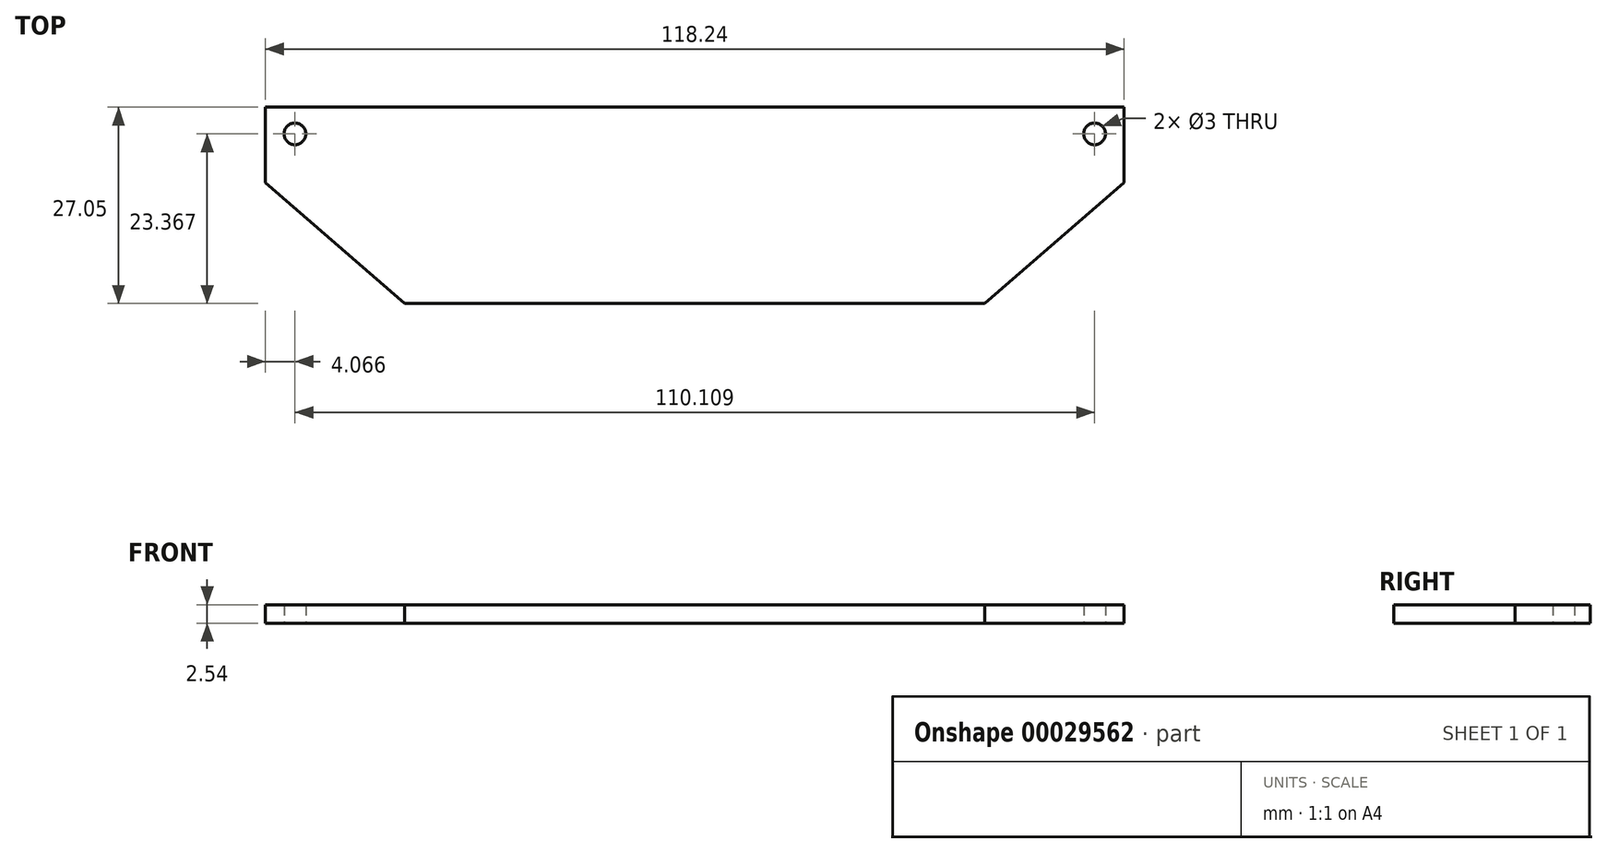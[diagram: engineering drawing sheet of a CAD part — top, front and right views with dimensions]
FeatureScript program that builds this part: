
annotation { "Feature Type Name" : "Feature", "Feature Type Description" : "" }
export const myFeature = defineFeature(function(context is Context, id is Id, definition is map)
    precondition{}
    {
        {
            var Q0;
            Q0=qCreatedBy(makeId("Top.planeOp"),FACE);
            var sketch = newSketch(context, id + "F0", { "sketchPlane" : qUnion([Q0])});
            skLineSegment(sketch, "E0", {"start": v(-59.12, 0) * mm, "end": v(59.12, 0) * mm});
            skPoint(sketch, "E1", {"position": v(0, 0) * mm});
            skLineSegment(sketch, "E2", {"start": v(-59.12, 0) * mm, "end": v(-59.12, -10.4) * mm});
            skLineSegment(sketch, "E3", {"start": v(-59.12, -10.4) * mm, "end": v(-39.94, -27.05) * mm});
            skLineSegment(sketch, "E4", {"start": v(-39.94, -27.05) * mm, "end": v(39.94, -27.05) * mm});
            skLineSegment(sketch, "E5", {"start": v(39.94, -27.05) * mm, "end": v(59.12, -10.4) * mm});
            skLineSegment(sketch, "E6", {"start": v(59.12, -10.4) * mm, "end": v(59.12, 0) * mm});
            skPoint(sketch, "E7", {"position": v(0, -27.05) * mm});
            skCircle(sketch, "E8", {"center": v(-55.05, -3.68) * mm, "radius": 1.5 * mm});
            skCircle(sketch, "E9", {"center": v(55.05, -3.68) * mm, "radius": 1.5 * mm});
            skSolve(sketch);
        }
        {
            var Q0;
            Q0 = qSketchRegion(id + "F0", true);
            extrude(context, id + "F1", {"entities" : qUnion([Q0]), "depth" : 2.54 * mm});
        }
    });
